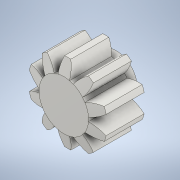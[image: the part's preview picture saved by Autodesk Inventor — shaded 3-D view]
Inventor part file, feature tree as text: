
AUTODESK INVENTOR PART (.ipt)
format: ipt  version: 2022 (Build 260153000, 153)  size: 535,040 bytes
history: native  units: mm (DEFAULTED — no unit token found)
features: sketch x6, extrude x4, plane x3, other x3, projected_geometry x2, revolve x1
ambient origin geometry x8: Origin, YZ Plane, XZ Plane, XY Plane, X Axis, Y Axis, Z Axis, Center Point
bodies: Solid1 (feature_tree)
feature tree (19):
  extrude  "Extrusion1"  Depth=6.35mm TaperAngle=0.0deg
  plane  "Work Plane1"
  plane  "Work Plane2"
  plane  "Work Plane3"
  other  "Spur Gear"
  extrude  "Extrusion2"  Depth=10.0mm TaperAngle=0.0deg
  extrude  "Extrusion3"  TaperAngle=0.0deg  [1 undecoded]
  revolve  "Revolution1"  [1 undecoded]
  extrude  "Extrusion4"  Depth=3.325mm
  sketch  "Sketch1"  dims[d0=11.961303mm d1=6.35mm d2=0.0mm]
  sketch  "Sketch2"  dims[d3=10.0mm d4=76.2mm d5=0.0mm]
  other  "Srf1"
  sketch  "Sketch3"  dims[d6=0.0mm d7=3.141593mm d9=0.0mm]
  sketch  "Sketch4"  dims[d14=0.0mm d15=23.75408mm d16=0.0mm]
  projected_geometry  "Projected Loop1"
  sketch  "Sketch5"  dims[d17=0.0mm d18=0.0mm d19=23.75408mm d20=3.325mm]
  sketch  "Sketch6"  dims[d21=0.0mm d22=0.0mm d23=6.35mm d24=1.5875mm d25=0.0mm d26=15.0deg d27=90.0deg d28=2.0mm d29=0.0mm]
  projected_geometry  "Projected Loop2"
  other  "Pitch Diameter"
note: 2 required parameter values undecoded (feature->parameter linkage not recoverable at this tier; creation-order binding heuristic only, values carry confidence <= 0.55)